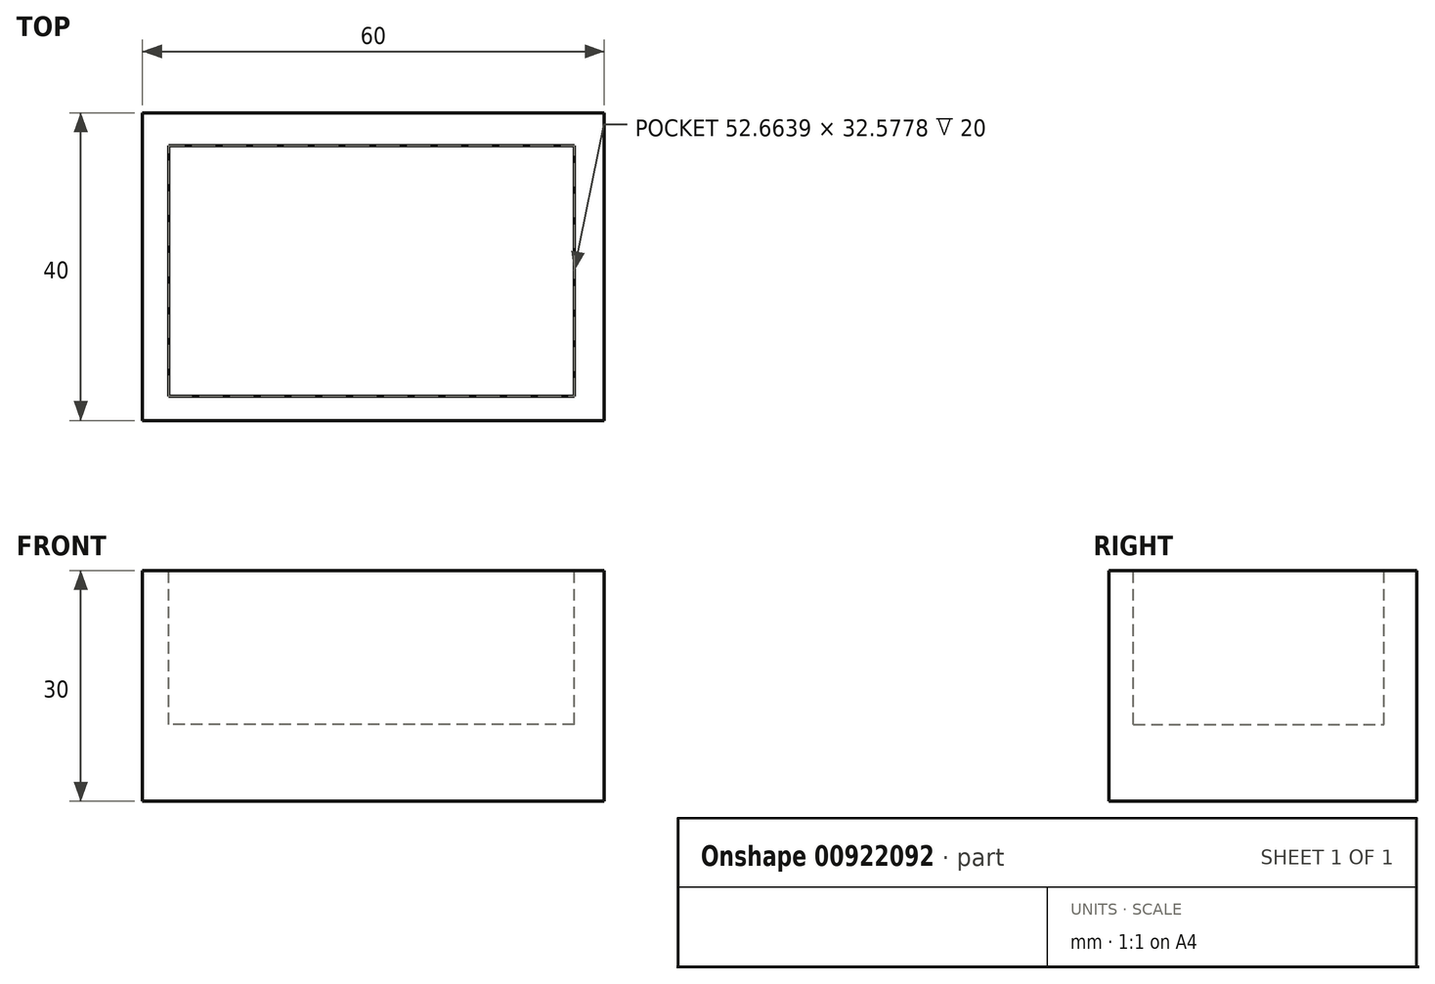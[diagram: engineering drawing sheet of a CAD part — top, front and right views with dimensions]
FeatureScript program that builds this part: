
annotation { "Feature Type Name" : "Feature", "Feature Type Description" : "" }
export const myFeature = defineFeature(function(context is Context, id is Id, definition is map)
    precondition{}
    {
        {
            var Q0;
            Q0=qCreatedBy(makeId("Top.planeOp"),FACE);
            var sketch = newSketch(context, id + "F0", { "sketchPlane" : qUnion([Q0])});
            skLineSegment(sketch, "E0", {"start": v(0, 0) * mm, "end": v(0, 40) * mm});
            skLineSegment(sketch, "E1", {"start": v(0, 40) * mm, "end": v(60, 40) * mm});
            skLineSegment(sketch, "E2", {"start": v(60, 40) * mm, "end": v(60, 0) * mm});
            skLineSegment(sketch, "E3", {"start": v(60, 0) * mm, "end": v(0, 0) * mm});
            skSolve(sketch);
        }
        {
            var Q0;
            Q0=makeQuery(id+"F0.imprint","IMPRINT",FACE,{"disambiguationData":[TD([[makeQuery(id+"F0.imprint","IMPRINT",EDGE,{"derivedFrom":sQuery(id+"F0.wireOp",EDGE,"E0")}),-1.0]])]});
            extrude(context, id + "F1", {"entities" : qUnion([Q0]), "depth" : 30 * mm, "offsetDistance" : 25 * mm});
        }
        {
            var Q0;
            Q0=makeQuery(id+"F1.opExtrude","CAP_FACE",FACE,{"disambiguationData":[OSD([sQuery(id+"F0.wireOp",EDGE,"E0"),sQuery(id+"F0.wireOp",EDGE,"E1"),sQuery(id+"F0.wireOp",EDGE,"E2"),sQuery(id+"F0.wireOp",EDGE,"E3")])],"isStart":false});
            var sketch = newSketch(context, id + "F2", { "sketchPlane" : qUnion([Q0])});
            skLineSegment(sketch, "E4", {"start": v(3.43, 3.18) * mm, "end": v(3.43, 35.76) * mm});
            skLineSegment(sketch, "E5", {"start": v(3.43, 35.76) * mm, "end": v(56.1, 35.76) * mm});
            skLineSegment(sketch, "E6", {"start": v(56.1, 35.76) * mm, "end": v(56.1, 3.18) * mm});
            skLineSegment(sketch, "E7", {"start": v(56.1, 3.18) * mm, "end": v(3.43, 3.18) * mm});
            skSolve(sketch);
        }
        {
            var Q0;
            Q0=makeQuery(id+"F2.imprint","IMPRINT",FACE,{"disambiguationData":[TD([[makeQuery(id+"F2.imprint","IMPRINT",EDGE,{"derivedFrom":sQuery(id+"F2.wireOp",EDGE,"E4")}),-1.0]])]});
            extrude(context, id + "F3", {"entities" : qUnion([Q0]), "operationType" : NewBodyOperationType.REMOVE, "oppositeDirection" : true, "depth" : 20 * mm, "offsetDistance" : 25 * mm});
        }
    });
